# Revit family: O10-S290-E LED 500 AC 840 BL_Vertical Wall
name_source: partatom
category: Lighting Fixtures
revit_build: Autodesk Revit 2016 (Build: 20151007_0715(x64)
units: mm (PartAtom-declared; Revit-internal decimal feet)

## family parameters
Always vertical = Yes
Cut with Voids When Loaded = No
Light Source = Yes
OmniClass Number = 23.80.70.00
OmniClass Title = Lighting
Part Type = Normal
Room Calculation Point = No
Round Connector Dimension = Use Diameter
Shared = No
Work Plane-Based = No

## types (1)
- O10-S290-E LED 500 AC 840 BL_Vertical Wall
    # ballast on a MCB16 type B fuse = 130
    # ballast on a MCB16 type C fuse = 176
    #Ballast = 1
    Apparent Load = 12 VA
    ArticleNumber = O10314300
    Body Material and Colour = Default
    Color Filter = 16777215
    Description = O10-S290-E LED 500 AC 840 BL
    Diameter = 290 mm  [stored 0.951444 ft]
    Dimming Lamp Color Temperature Shift = Incandescent Lamp Curve
    EANNo = 4741145295499
    Emit Shape Visible in Rendering = Yes
    Emit from Circle Diameter = 290 mm  [stored 0.951444 ft]
    Expired = 0
    Frequency = 50 Hz
    FrequencyMax = 60 Hz
    Glamox Category = Outdoor
    Glamox Family = O10-S290
    Glamox Mounting = Surface
    GlobalTradeItemNumber = 4741145295499
    Height = 149 mm
    IFC Classification = Light Fixture
    IPClass = 66
    IP_Code = 66
    Lamp = LED
    LightFixtureMountingType = SURFACE
    LightFixturePlacingType = WALL
    LumDiameter = 290 mm  [stored 0.951444 ft]
    MFArtNo = O10314300
    MaintenanceFactor = 0
    Manufacturer = Glamox
    Maximum TA = 40
    ModelLabel = O10-S290-E LED 500 AC 840 BL
    ModelReference = O10-S290
    NominalFrequencyRange = 50 Hz
    Number of Poles = 1
    Photometric Web File = O10-S290-E-LED-500-840.ies
    Power Factor = 0.98
    PowerFactor = 98.00%
    Radius = 145 mm  [stored 0.475722 ft]
    RatedVoltage = 220 V
    Specification = Outdoor product, in Aluminium, for Surface/Wall mounting, impact classification IK10, IP66, light source LED, lumen out 435lm, ballast type AC, with light source type CRI>80, 4000K, with Polycarbonate diffuser.
    Termination = 5x2x2,5 PI
    Tilt Angle = 90.00°
    Top Radius = 113 mm
    Total Load = 12 W
    TotalWattage = 12 W
    URL Denmark = http://glamox.com
    URL Estonia = http://glamox.com
    URL Finland = http://glamox.com
    URL Germany = http://glamox.com
    URL Ireland = http://glamox.com
    URL Norway = http://glamox.com
    URL Other = http://glamox.com
    URL Russia = http://glamox.com
    URL Sweden = http://glamox.com
    URL UK = http://glamox.com
    UpdateDate = 27.04.2018 10:30:07
    Voltage = 220 V
    VoltageMax = 240 V

note: [stored X ft] marks values corroborated as IEEE doubles in the binary element streams (Revit-internal decimal feet)

## geometry (parser evidence)
native form markers: Blend x8, Sweep x2
no freeform markers — native parametric forms only
